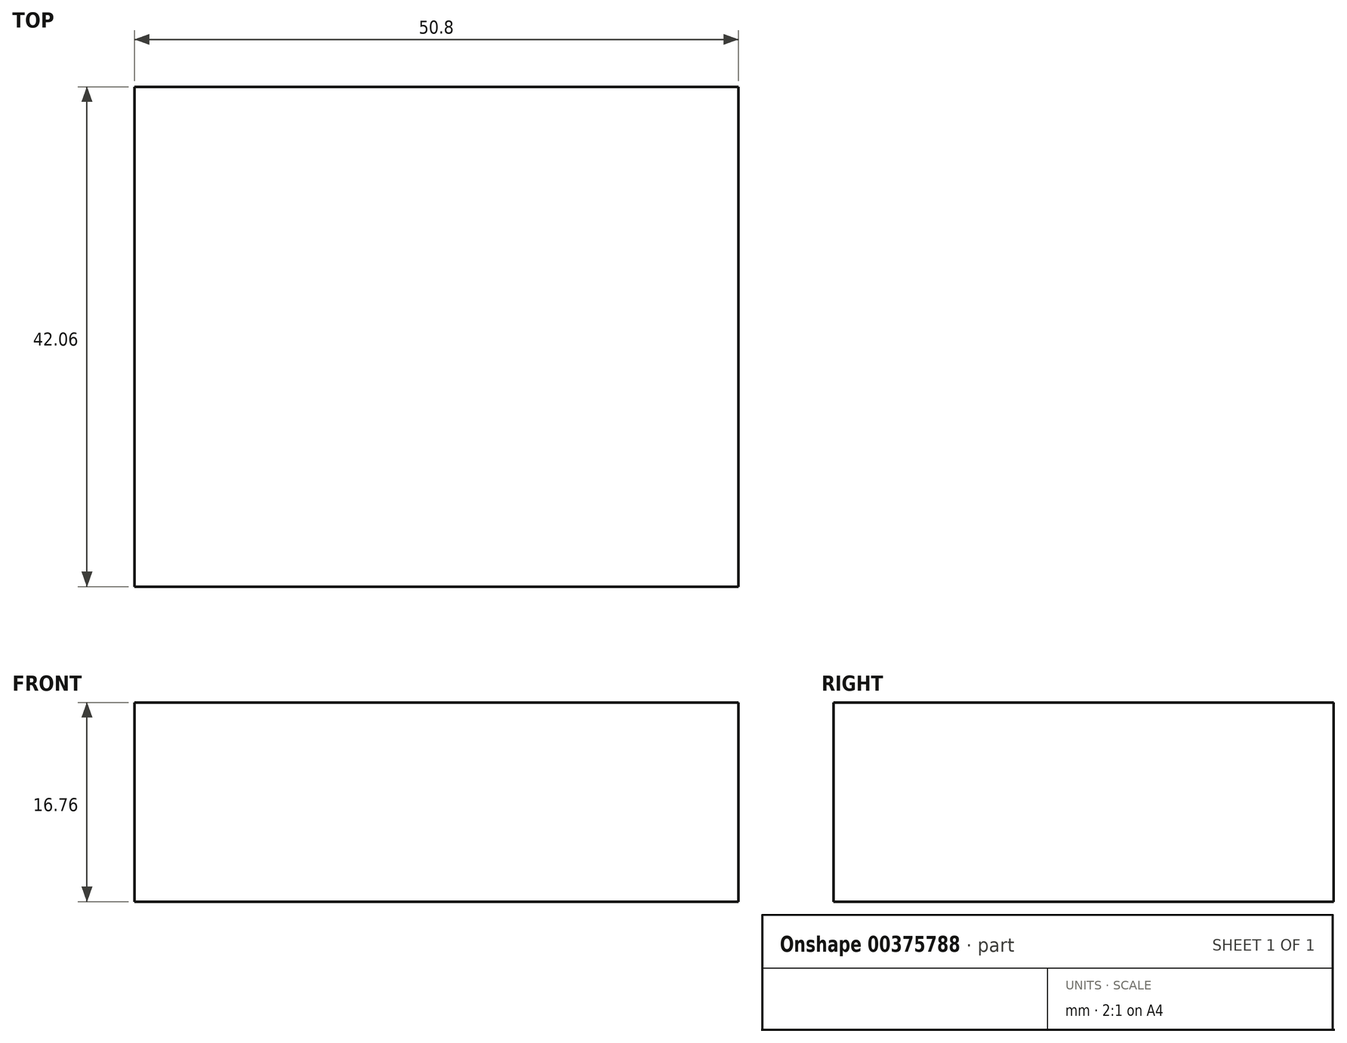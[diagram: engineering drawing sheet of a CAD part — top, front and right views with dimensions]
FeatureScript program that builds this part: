
annotation { "Feature Type Name" : "Feature", "Feature Type Description" : "" }
export const myFeature = defineFeature(function(context is Context, id is Id, definition is map)
    precondition{}
    {
        {
            var Q0;
            Q0=qCreatedBy(makeId("Right.planeOp"),FACE);
            var sketch = newSketch(context, id + "F0", { "sketchPlane" : qUnion([Q0])});
            skLineSegment(sketch, "E0.bottom", {"start": v(21.03, 8.38) * mm, "end": v(-21.03, 8.38) * mm});
            skLineSegment(sketch, "E0.top", {"start": v(21.03, -8.38) * mm, "end": v(-21.03, -8.38) * mm});
            skLineSegment(sketch, "E0.left", {"start": v(21.03, 8.38) * mm, "end": v(21.03, -8.38) * mm});
            skLineSegment(sketch, "E0.right", {"start": v(-21.03, 8.38) * mm, "end": v(-21.03, -8.38) * mm});
            skPoint(sketch, "E0.middle", {"position": v(0, 0) * mm});
            skLineSegment(sketch, "E1.bottom", {"start": v(6.1, 11.43) * mm, "end": v(-6.1, 11.43) * mm});
            skLineSegment(sketch, "E1.top", {"start": v(6.1, 5.33) * mm, "end": v(-6.1, 5.33) * mm});
            skLineSegment(sketch, "E1.left", {"start": v(6.1, 11.43) * mm, "end": v(6.1, 5.33) * mm});
            skLineSegment(sketch, "E1.right", {"start": v(-6.1, 11.43) * mm, "end": v(-6.1, 5.33) * mm});
            skPoint(sketch, "E1.middle", {"position": v(0, 8.38) * mm});
            skLineSegment(sketch, "E2.MirrorCS", {"start": v(-6.1, -11.43) * mm, "end": v(-6.1, -5.33) * mm});
            skLineSegment(sketch, "E3.MirrorCS", {"start": v(6.1, -11.43) * mm, "end": v(6.1, -5.33) * mm});
            skLineSegment(sketch, "E4.MirrorCS", {"start": v(6.1, -11.43) * mm, "end": v(-6.1, -11.43) * mm});
            skLineSegment(sketch, "E5.MirrorCS", {"start": v(6.1, -5.33) * mm, "end": v(-6.1, -5.33) * mm});
            skPoint(sketch, "E6.MirrorP", {"position": v(0, -8.38) * mm});
            skSolve(sketch);
        }
        {
            var Q0;
            {var subQ5=sQuery(id+"F0.wireOp",EDGE,"E1.top");Q0=makeQuery(id+"F0.imprint","IMPRINT",FACE,{"disambiguationData":[TD([[makeQuery(id+"F0.imprint","IMPRINT",EDGE,{"derivedFrom":subQ5}),-1.0]])]});}
            var Q1;
            {var subQ10=sQuery(id+"F0.wireOp",EDGE,"E0.left");Q1=makeQuery(id+"F0.imprint","IMPRINT",FACE,{"disambiguationData":[TD([[makeQuery(id+"F0.imprint","IMPRINT",EDGE,{"derivedFrom":subQ10}),-1.0]])]});}
            var Q2;
            {var subQ0=sQuery(id+"F0.wireOp",EDGE,"E5.MirrorCS");Q2=makeQuery(id+"F0.imprint","IMPRINT",FACE,{"disambiguationData":[TD([[makeQuery(id+"F0.imprint","IMPRINT",EDGE,{"derivedFrom":subQ0}),1.0]])]});}
            extrude(context, id + "F1", {"entities" : qUnion([Q0, Q1, Q2]), "depth" : 50.8 * mm});
        }
    });
